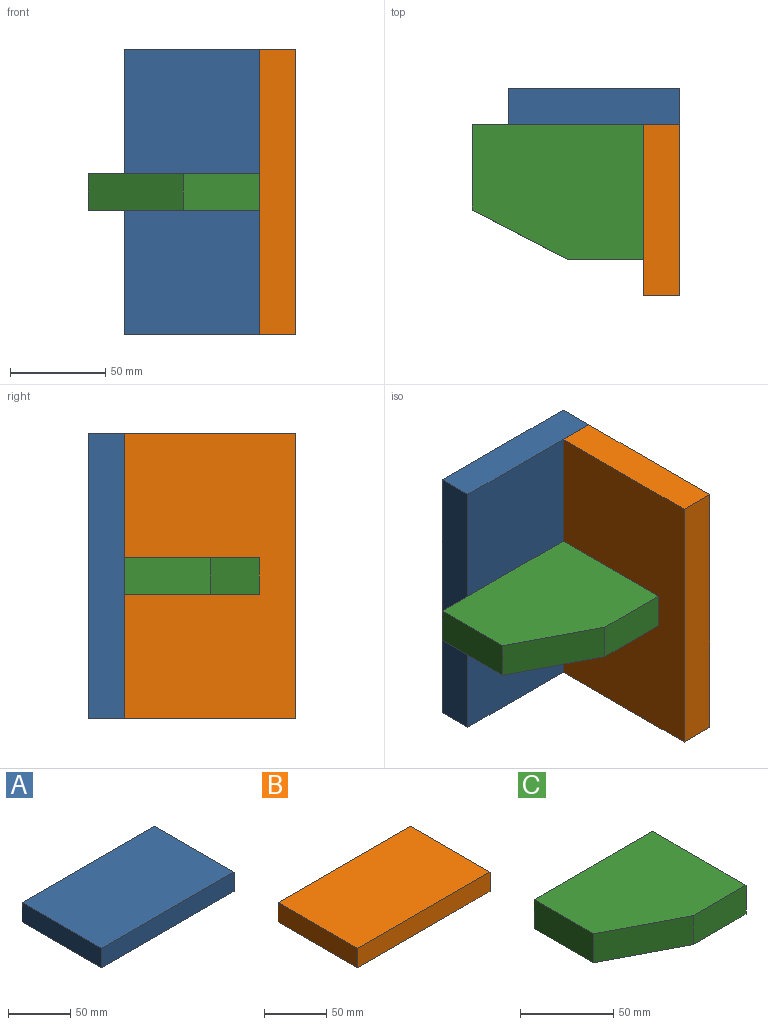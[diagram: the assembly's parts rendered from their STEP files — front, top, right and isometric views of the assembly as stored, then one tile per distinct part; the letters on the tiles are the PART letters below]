
ASSEMBLY  parts=3 mates=2
PART A: 6 faces, bbox 150x90x19 mm
  f0: plane 150x19mm, normal (0,-1,0), area 2850mm2, adj f1,f3,f4,f5
  f1: plane 90x19mm, normal (1,0,0), area 1710mm2, adj f0,f2,f4,f5
  f2: plane 150x19mm, normal (0,1,0), area 2850mm2, adj f1,f3,f4,f5
  f3: plane 90x19mm, normal (-1,0,0), area 1710mm2, adj f0,f2,f4,f5
  f4: plane 150x90mm, normal (0,0,1), area 13500mm2, adj f0,f1,f2,f3
  f5: plane 150x90mm, normal (0,0,-1), area 13500mm2, adj f0,f1,f2,f3
PART B: 6 faces, bbox 150x90x19 mm
  f0: plane 90x19mm, normal (-1,0,0), area 1710mm2, adj f1,f3,f4,f5
  f1: plane 150x19mm, normal (0,-1,0), area 2850mm2, adj f0,f2,f4,f5
  f2: plane 90x19mm, normal (1,0,0), area 1710mm2, adj f1,f3,f4,f5
  f3: plane 150x19mm, normal (0,1,0), area 2850mm2, adj f0,f2,f4,f5
  f4: plane 150x90mm, normal (0,0,1), area 13500mm2, adj f0,f1,f2,f3
  f5: plane 150x90mm, normal (0,0,-1), area 13500mm2, adj f0,f1,f2,f3
PART C: 7 faces, bbox 90x71x19 mm
  f0: plane 71x19mm, normal (1,0,0), area 1349mm2, adj f1,f4,f5,f6
  f1: plane 90x19mm, normal (0,1,0), area 1710mm2, adj f0,f2,f5,f6
  f2: plane 45x19mm, normal (-1,0,0), area 855mm2, adj f1,f3,f5,f6
  f3: plane 50x26mm, normal (-0.46,-0.89,0), area 1070.8mm2, adj f2,f4,f5,f6
  f4: plane 40x19mm, normal (0,-1,0), area 760mm2, adj f0,f3,f5,f6
  f5: plane 90x71mm, normal (0,0,1), area 5740mm2, adj f0,f1,f2,f3,f4
  f6: plane 90x71mm, normal (0,0,-1), area 5740mm2, adj f0,f1,f2,f3,f4
PLACE A rot(axis=(-0.58,0.58,0.58),120deg) t=(-274.94,30.14,21.54)mm
PLACE B rot(axis=(0,1,0),90deg) t=(-293.94,-59.86,203.68)mm
PLACE C t=(-242.92,60.48,119.18)mm
MATE fastened C.f0 <-> B.f5  axis (1,0,0) through (-293.94,30.14,128.68)mm
MATE fastened B.f3 <-> A.f5  axis (0,1,0) through (-274.94,30.14,203.68)mm
